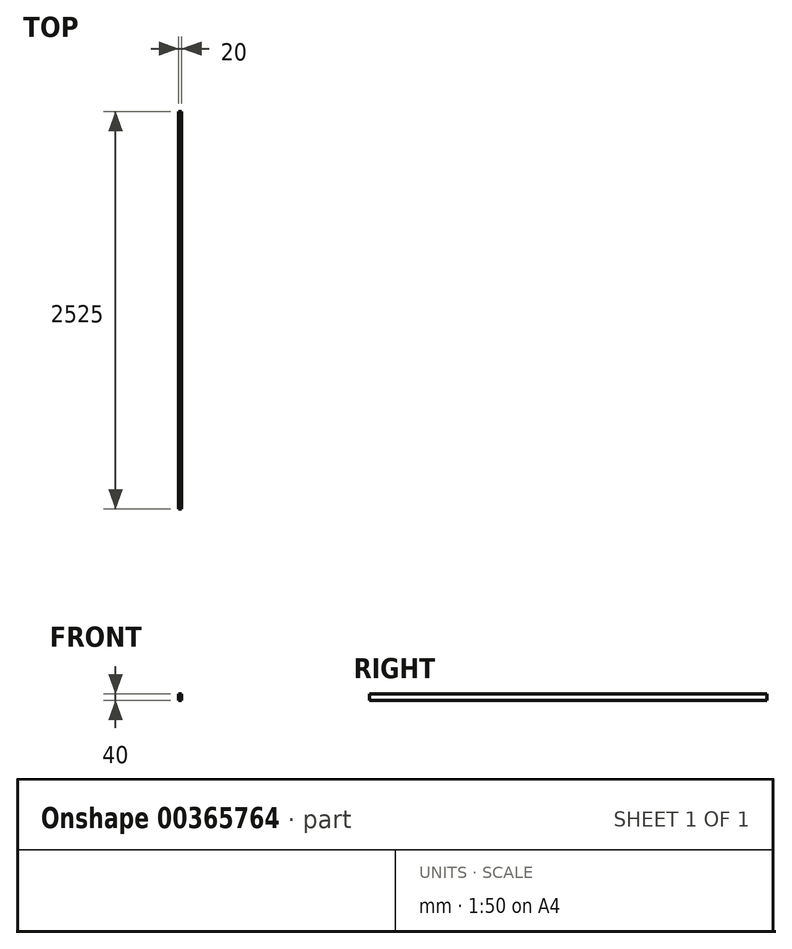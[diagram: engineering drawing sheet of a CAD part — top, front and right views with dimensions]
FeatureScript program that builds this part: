
annotation { "Feature Type Name" : "Feature", "Feature Type Description" : "" }
export const myFeature = defineFeature(function(context is Context, id is Id, definition is map)
    precondition{}
    {
        {
            var Q0;
            Q0=qCreatedBy(makeId("Front.planeOp"),FACE);
            var sketch = newSketch(context, id + "F0", { "sketchPlane" : qUnion([Q0])});
            skLineSegment(sketch, "E0.bottom", {"start": v(-10, 20) * mm, "end": v(10, 20) * mm});
            skLineSegment(sketch, "E0.top", {"start": v(-10, -20) * mm, "end": v(10, -20) * mm});
            skLineSegment(sketch, "E0.left", {"start": v(-10, 20) * mm, "end": v(-10, -20) * mm});
            skLineSegment(sketch, "E0.right", {"start": v(10, 20) * mm, "end": v(10, -20) * mm});
            skPoint(sketch, "E0.middle", {"position": v(0, 0) * mm});
            skSolve(sketch);
        }
        {
            var Q0;
            Q0=makeQuery(id+"F0.imprint","IMPRINT",FACE,{"disambiguationData":[TD([[makeQuery(id+"F0.imprint","IMPRINT",EDGE,{"derivedFrom":sQuery(id+"F0.wireOp",EDGE,"E0.bottom")}),-1.0]])]});
            extrude(context, id + "F1", {"entities" : qUnion([Q0]), "depth" : 2525 * mm});
        }
    });
